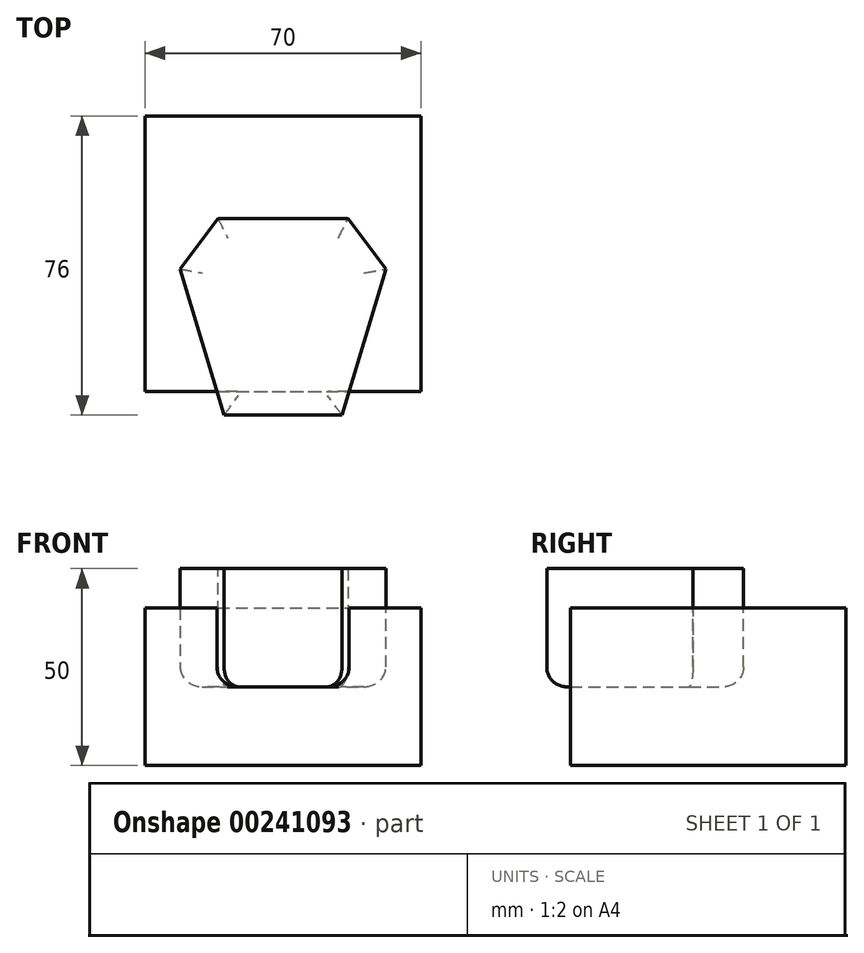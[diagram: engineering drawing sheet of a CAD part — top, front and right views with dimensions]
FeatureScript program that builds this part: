
annotation { "Feature Type Name" : "Feature", "Feature Type Description" : "" }
export const myFeature = defineFeature(function(context is Context, id is Id, definition is map)
    precondition{}
    {
        {
            var Q0;
            Q0=qCreatedBy(makeId("Top.planeOp"),FACE);
            var sketch = newSketch(context, id + "F0", { "sketchPlane" : qUnion([Q0])});
            skLineSegment(sketch, "E0", {"start": v(0, 100.57) * mm, "end": v(0, -68.31) * mm, "construction": true});
            skLineSegment(sketch, "E1", {"start": v(0, 0) * mm, "end": v(-15, 0) * mm});
            skLineSegment(sketch, "E2", {"start": v(-15, 0) * mm, "end": v(-30, 50) * mm});
            skLineSegment(sketch, "E3", {"start": v(-30, 50) * mm, "end": v(0, 50) * mm});
            skLineSegment(sketch, "E4.MirrorCS", {"start": v(30, 50) * mm, "end": v(0, 50) * mm});
            skLineSegment(sketch, "E5.MirrorCS", {"start": v(15, 0) * mm, "end": v(30, 50) * mm});
            skLineSegment(sketch, "E6.MirrorCS", {"start": v(0, 0) * mm, "end": v(15, 0) * mm});
            skSolve(sketch);
        }
        {
            var Q0;
            Q0 = qSketchRegion(id + "F0", true);
            extrude(context, id + "F1", {"entities" : qUnion([Q0]), "depth" : 30 * mm});
        }
        {
            var Q0;
            Q0=makeQuery(id+"F1.opExtrude","SWEPT_EDGE",EDGE,{"disambiguationData":[OSD([sQuery(id+"F0.wireOp",EDGE,"E2"),sQuery(id+"F0.wireOp",EDGE,"E3")])]});
            var Q1;
            Q1=makeQuery(id+"F1.opExtrude","SWEPT_EDGE",EDGE,{"disambiguationData":[OSD([sQuery(id+"F0.wireOp",EDGE,"E4.MirrorCS"),sQuery(id+"F0.wireOp",EDGE,"E5.MirrorCS")])]});
            chamfer(context, id + "F2", {"entities" : qUnion([Q0, Q1]), "width" : 10 * mm, "tangentPropagation" : true});
        }
        {
            var Q0;
            Q0=makeQuery(id+"F1.opExtrude","CAP_FACE",FACE,{"disambiguationData":[OSD([sQuery(id+"F0.wireOp",EDGE,"E1"),sQuery(id+"F0.wireOp",EDGE,"E2"),sQuery(id+"F0.wireOp",EDGE,"E3"),sQuery(id+"F0.wireOp",EDGE,"E4.MirrorCS"),sQuery(id+"F0.wireOp",EDGE,"E5.MirrorCS"),sQuery(id+"F0.wireOp",EDGE,"E6.MirrorCS")])],"isStart":true});
            fillet(context, id + "F3", {"entities" : qUnion([Q0]), "radius" : 5 * mm, "tangentPropagation" : true, "allowEdgeOverflow" : false});
        }
        {
            var Q0;
            Q0=qCreatedBy(makeId("Top.planeOp"),FACE);
            var sketch = newSketch(context, id + "F4", { "sketchPlane" : qUnion([Q0])});
            skLineSegment(sketch, "E7.bottom", {"start": v(-35, 6) * mm, "end": v(35, 6) * mm});
            skLineSegment(sketch, "E7.top", {"start": v(-35, 76) * mm, "end": v(35, 76) * mm});
            skLineSegment(sketch, "E7.left", {"start": v(-35, 6) * mm, "end": v(-35, 76) * mm});
            skLineSegment(sketch, "E7.right", {"start": v(35, 6) * mm, "end": v(35, 76) * mm});
            skLineSegment(sketch, "E8", {"start": v(0, 114.32) * mm, "end": v(0, -45.79) * mm, "construction": true});
            skPoint(sketch, "E9", {"position": v(0, 6) * mm});
            skSolve(sketch);
        }
        {
            var Q0;
            Q0 = qSketchRegion(id + "F4", true);
            extrude(context, id + "F5", {"entities" : qUnion([Q0]), "depth" : 20 * mm, "hasSecondDirection" : true, "secondDirectionOppositeDirection" : true, "secondDirectionDepth" : 20 * mm});
        }
        {
            var Q0;
            Q0=makeQuery(id+"F1.opExtrude","SWEPT_BODY",BODY,{"disambiguationData":[OSD([sQuery(id+"F0.wireOp",EDGE,"E1"),sQuery(id+"F0.wireOp",EDGE,"E2"),sQuery(id+"F0.wireOp",EDGE,"E3"),sQuery(id+"F0.wireOp",EDGE,"E4.MirrorCS"),sQuery(id+"F0.wireOp",EDGE,"E5.MirrorCS"),sQuery(id+"F0.wireOp",EDGE,"E6.MirrorCS")])]});
            var Q1;
            Q1=makeQuery(id+"F5.opExtrude","SWEPT_BODY",BODY,{"disambiguationData":[OSD([sQuery(id+"F4.wireOp",EDGE,"E7.bottom"),sQuery(id+"F4.wireOp",EDGE,"E7.top"),sQuery(id+"F4.wireOp",EDGE,"E7.left"),sQuery(id+"F4.wireOp",EDGE,"E7.right")])]});
            var Q2;
            Q2=makeQuery(id+"F1.opExtrude","SWEPT_FACE",FACE,{"disambiguationData":[OSD([sQuery(id+"F0.wireOp",EDGE,"E2")])]});
            var Q3;
            Q3=makeQuery(id+"F1.opExtrude","SWEPT_FACE",FACE,{"disambiguationData":[OSD([sQuery(id+"F0.wireOp",EDGE,"E1"),sQuery(id+"F0.wireOp",EDGE,"E6.MirrorCS")])]});
            var Q4;
            Q4=makeQuery(id+"F1.opExtrude","SWEPT_FACE",FACE,{"disambiguationData":[OSD([sQuery(id+"F0.wireOp",EDGE,"E5.MirrorCS")])]});
            var Q5;
            Q5=makeQuery(id+"F2.opChamfer","BLEND_FACE",FACE,{"disambiguationData":[OSD([sQuery(id+"F0.wireOp",EDGE,"E4.MirrorCS"),sQuery(id+"F0.wireOp",EDGE,"E5.MirrorCS")])]});
            var Q6;
            Q6=makeQuery(id+"F1.opExtrude","SWEPT_FACE",FACE,{"disambiguationData":[OSD([sQuery(id+"F0.wireOp",EDGE,"E3"),sQuery(id+"F0.wireOp",EDGE,"E4.MirrorCS")])]});
            booleanBodies(context, id + "F6", {"operationType" : BooleanOperationType.SUBTRACTION, "tools" : qUnion([Q0]), "targets" : qUnion([Q1]), "entitiesToOffset" : qUnion([Q2, Q3, Q4, Q5, Q6]), "keepTools" : true});
        }
    });
